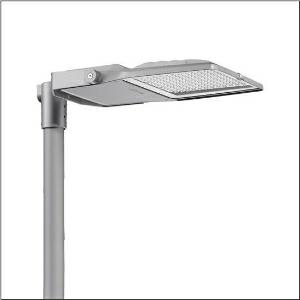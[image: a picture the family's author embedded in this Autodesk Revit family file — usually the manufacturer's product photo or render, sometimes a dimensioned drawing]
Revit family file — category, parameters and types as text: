
# Revit family: floodlight_fl_21_iq_midi___pl61_5xa7782f4c3a_0871
name_source: partatom
category: Lighting Fixtures
units: mm (PartAtom-declared; Revit-internal decimal feet)

## family parameters
Cut with Voids When Loaded = No
Host = Face
Light Source = No
Part Type = Normal
Room Calculation Point = No
Round Connector Dimension = Use Diameter
Shared = No

## types (1)
- --- (1 x LED, 36650 lm, 270.2 W, 4000K)
    Apparent Load = 270 VA
    CIE Flux Codes = 33 65 98 100 100
    Color Rendering = 70
    Color Temperature = 4000K
    Default Elevation = 1800 mm
    Description = Floodlight FL 21 iQ midi, floodlight, primary light control with lens, of PMMA, primary optical cover: protective disc, of toughened safety glass, transparent, light distribution: PL61, light emission: direct distribution, installation type: surface-mounted, LED, High Power LED, rated luminous flux: 36.650lm, luminous efficacy: 136lm/W, light colour: 740, colour temperature: 4000K, control gear: iQ Street-Remote/DALI, control: optimised constant luminous flux control (CLO 2.0), Desk-Remote (wireless, voltage-free reading and setting of iQ features in the workshop via application-optimized NFC function/RFID function), Smart-Wire, Night-Set, Temp-Guard, Auto-Match, Street-Remote, with terminal, 6-pole, mains connection: 220..240V, AC, 50/60Hz, start of lifetime: 270W, end of service life: 287W, reduction: 118W, luminaire housing, of diecast aluminium, powder-coated, Siteco® metallic grey (DB 702S), corrosivity category C5 mid according to DIN EN ISO 12944, suitable for swimming pools, chlorine-resistant, sealing non-destructively replaceable, please order mast flange separately, mast bracket, of steel, galvanised, powder-coated, Siteco® metallic grey (DB 702S), protection rating (complete): IP66, insulation class (complete): insulation class II (safety insulation), certification: CE, ENEC, VDE, protection symbol: D, impact resistance: IK08, permissible operating ambient temperature: -40..+40°C, permissible operating ambient temperature for outdoor applications: -40..+50°C, standard: DIN EN 12944, LABS conformity tested according to VDMA 24364:2018-05, packaging unit: 1 piece

Light Distribution: PL61
    Height = 76 mm
    Lamp = 1 x LED
    Lamp Light Flux = 36650 lm
    Lamp Power = 270.2 W
    Lamp count = 1
    Length = 657 mm
    Luminous efficacy = 136 lm/W
    Manufacturer = Siteco
    ModVariant = No
    Model = 5XA7782F4C3A
    Number of Poles = 1
    OnlyDefault = Yes
    Power Factor = 1
    Product Name = Floodlight FL 21 iQ midi | PL61
    Product group = floodlight | pylon annexe
    ProductGroupID = 6200
    Protection Class = Protection class II
    Protection Degree = IP 66
    RLX_Detail_Level = 1
    RLX_Emergency_Light_Flux = 0 lm
    RLX_Emergency_Type = 0
    RLX_Emergency_Type_DB = No
    RlxData = <blob elided: 153945 chars, md5=359de09c>
    Socket = socket
    Standby Power = 0 W
    System Light Flux = 36650 lm
    System Power = 270 W
    Type Comments = factory setting: luminous flux: 100 % | dim-lin: 254 | 620 mA
    Type Image = l_1007123.jpg
    URL = http://relux.com
    VarID = @adj_108184
    Voltage = 0 V
    Weight = 0.00 kg
    Width = 442 mm

## geometry (parser evidence)
native form markers: Blend x4, Sweep x14
no freeform markers — native parametric forms only
